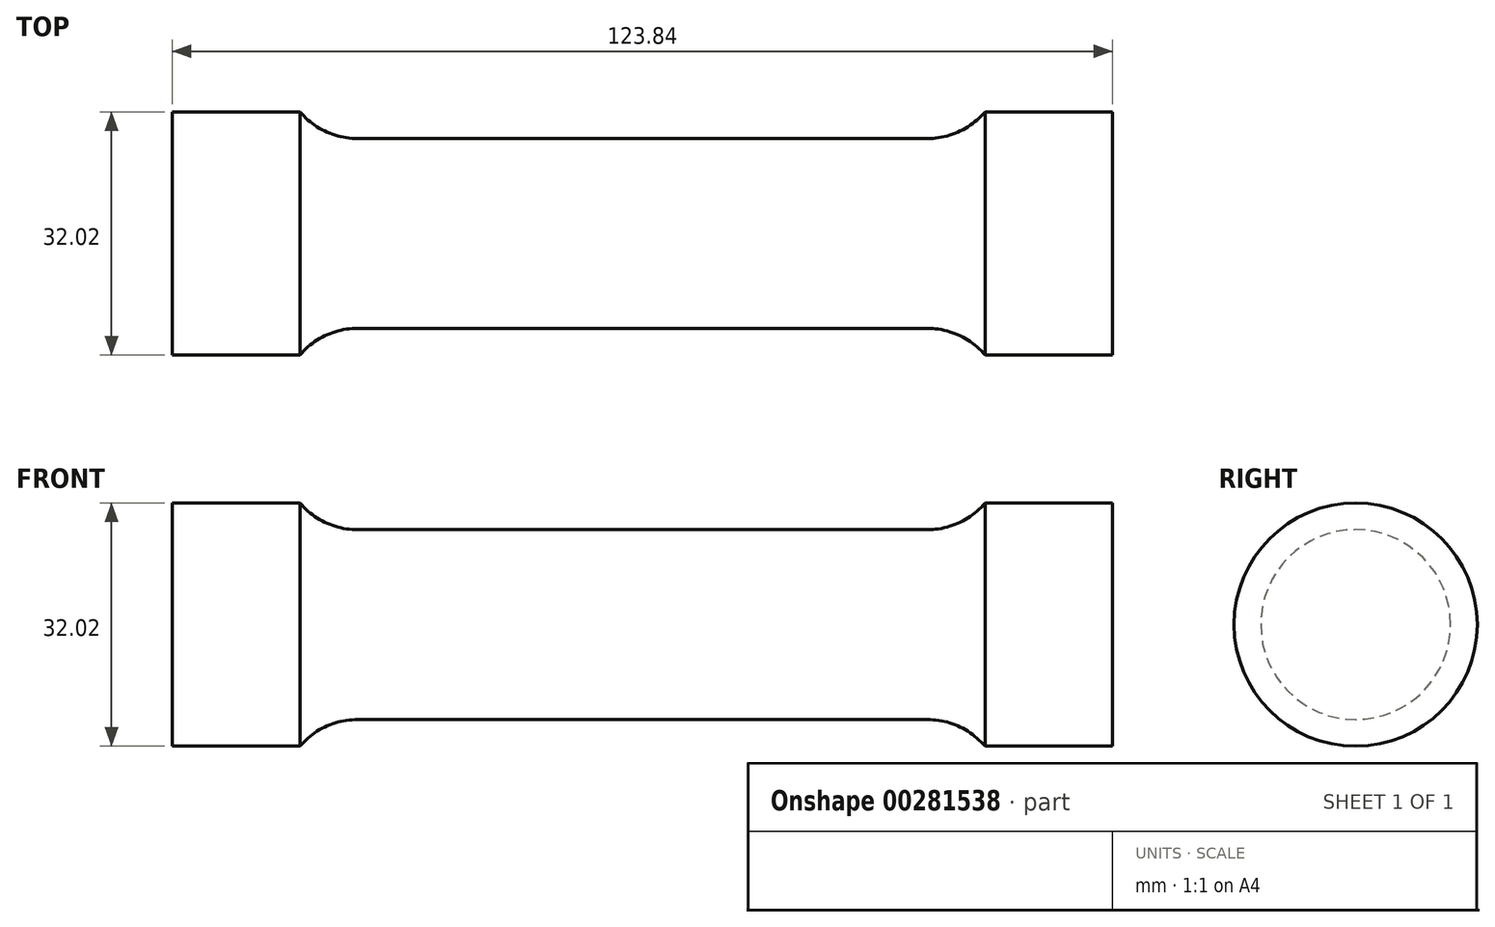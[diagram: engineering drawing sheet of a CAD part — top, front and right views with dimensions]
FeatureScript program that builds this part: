
annotation { "Feature Type Name" : "Feature", "Feature Type Description" : "" }
export const myFeature = defineFeature(function(context is Context, id is Id, definition is map)
    precondition{}
    {
        {
            var Q0;
            Q0=qCreatedBy(makeId("Front.planeOp"),FACE);
            var sketch = newSketch(context, id + "F0", { "sketchPlane" : qUnion([Q0])});
            skLineSegment(sketch, "E0", {"start": v(0, 12.5) * mm, "end": v(37.5, 12.5) * mm});
            skArc(sketch, "E1", {"start": v(37.5, 12.5) * mm, "mid": v(41.7, 13.42) * mm, "end": v(45.1, 16.01) * mm});
            skLineSegment(sketch, "E2", {"start": v(45.1, 16.01) * mm, "end": v(61.92, 16.01) * mm});
            skLineSegment(sketch, "E3", {"start": v(61.92, 16.01) * mm, "end": v(61.92, 0) * mm});
            skLineSegment(sketch, "E4.MirrorCS", {"start": v(0, 12.5) * mm, "end": v(-37.5, 12.5) * mm});
            skLineSegment(sketch, "E5.MirrorCS", {"start": v(-61.92, 16.01) * mm, "end": v(-61.92, 0) * mm});
            skLineSegment(sketch, "E6.MirrorCS", {"start": v(-45.1, 16.01) * mm, "end": v(-61.92, 16.01) * mm});
            skArc(sketch, "E7.MirrorCS", {"start": v(-37.5, 12.5) * mm, "mid": v(-41.7, 13.42) * mm, "end": v(-45.1, 16.01) * mm});
            skLineSegment(sketch, "E8", {"start": v(-61.92, 0) * mm, "end": v(61.92, 0) * mm});
            skSolve(sketch);
        }
        {
            var Q0;
            Q0 = qSketchRegion(id + "F0", true);
            var Q1;
            Q1=sQuery(id+"F0.wireOp",EDGE,"E8");
            revolve(context, id + "F1", {"entities" : qUnion([Q0]), "axis" : qUnion([Q1]), "revolveType" : RevolveType.FULL});
        }
    });
